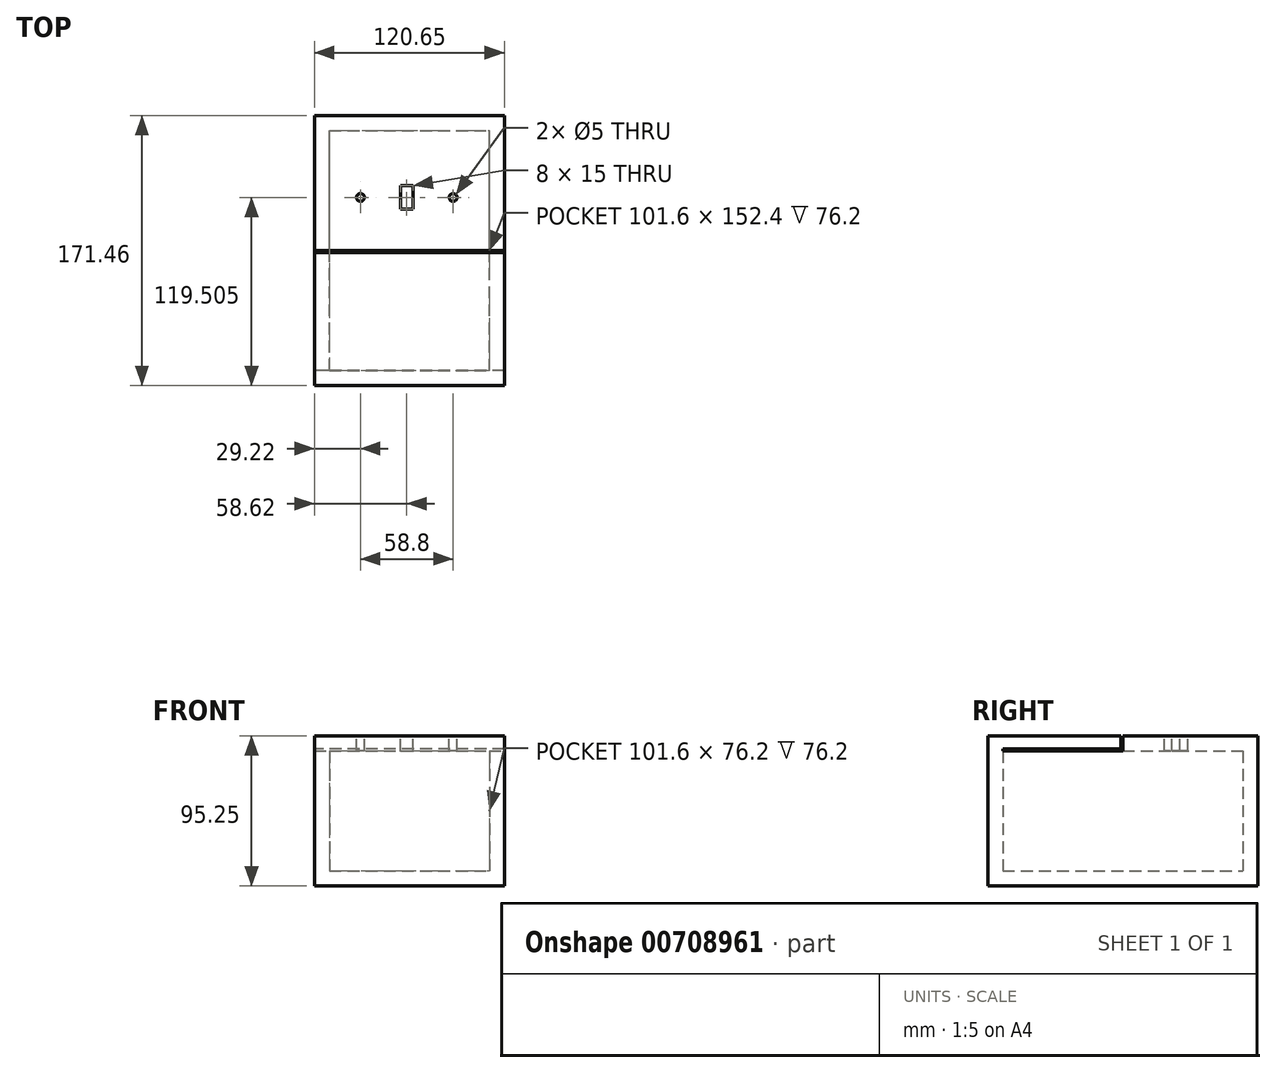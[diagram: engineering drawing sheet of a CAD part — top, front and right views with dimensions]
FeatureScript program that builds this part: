
annotation { "Feature Type Name" : "Feature", "Feature Type Description" : "" }
export const myFeature = defineFeature(function(context is Context, id is Id, definition is map)
    precondition{}
    {
        {
            var Q0;
            Q0=qCreatedBy(makeId("Front.planeOp"),FACE);
            var sketch = newSketch(context, id + "F0", { "sketchPlane" : qUnion([Q0])});
            skLineSegment(sketch, "E0.bottom", {"start": v(-49.1, 38.1) * mm, "end": v(52.5, 38.1) * mm});
            skLineSegment(sketch, "E0.top", {"start": v(-49.1, -38.1) * mm, "end": v(52.5, -38.1) * mm});
            skLineSegment(sketch, "E0.left", {"start": v(-49.1, 38.1) * mm, "end": v(-49.1, -38.1) * mm});
            skLineSegment(sketch, "E0.right", {"start": v(52.5, 38.1) * mm, "end": v(52.5, -38.1) * mm});
            skLineSegment(sketch, "E1.bottom", {"start": v(-58.62, 47.62) * mm, "end": v(62.03, 47.62) * mm});
            skLineSegment(sketch, "E1.top", {"start": v(-58.62, -47.63) * mm, "end": v(62.03, -47.63) * mm});
            skLineSegment(sketch, "E1.left", {"start": v(-58.62, 47.62) * mm, "end": v(-58.62, -47.63) * mm});
            skLineSegment(sketch, "E1.right", {"start": v(62.03, 47.62) * mm, "end": v(62.03, -47.63) * mm});
            skSolve(sketch);
        }
        {
            var Q0;
            Q0 = qSketchRegion(id + "F0", true);
            extrude(context, id + "F1", {"entities" : qUnion([Q0]), "depth" : 152.4 * mm, "offsetDistance" : 25.4 * mm});
        }
        {
            var Q0;
            Q0=makeQuery(id+"F1.opExtrude","SWEPT_FACE",FACE,{"disambiguationData":[OSD([sQuery(id+"F0.wireOp",EDGE,"E1.left")])]});
            var sketch = newSketch(context, id + "F2", { "sketchPlane" : qUnion([Q0])});
            skLineSegment(sketch, "E2.bottom", {"start": v(0, 47.63) * mm, "end": v(-9.53, 47.63) * mm});
            skLineSegment(sketch, "E2.top", {"start": v(0, -47.63) * mm, "end": v(-9.52, -47.63) * mm});
            skLineSegment(sketch, "E2.left", {"start": v(0, 47.63) * mm, "end": v(0, -47.63) * mm});
            skLineSegment(sketch, "E2.right", {"start": v(-9.53, 47.63) * mm, "end": v(-9.52, -47.63) * mm});
            skLineSegment(sketch, "E3.bottom", {"start": v(152.4, 47.63) * mm, "end": v(161.93, 47.63) * mm});
            skLineSegment(sketch, "E3.top", {"start": v(152.4, -47.63) * mm, "end": v(161.93, -47.63) * mm});
            skLineSegment(sketch, "E3.left", {"start": v(152.4, 47.63) * mm, "end": v(152.4, -47.63) * mm});
            skLineSegment(sketch, "E3.right", {"start": v(161.93, 47.63) * mm, "end": v(161.93, -47.63) * mm});
            skSolve(sketch);
        }
        {
            var Q0;
            Q0 = qSketchRegion(id + "F2", true);
            extrude(context, id + "F3", {"entities" : qUnion([Q0]), "operationType" : NewBodyOperationType.ADD, "oppositeDirection" : true, "depth" : 120.65 * mm, "offsetDistance" : 25.4 * mm});
        }
        {
            var Q0;
            Q0=makeQuery(id+"F3.boolean.opBoolean","MERGE",FACE,{"derivedFrom":[makeQuery(id+"F1.opExtrude","SWEPT_FACE",FACE,{"disambiguationData":[OSD([sQuery(id+"F0.wireOp",EDGE,"E1.bottom")])]}),makeQuery(id+"F3.opExtrude","SWEPT_FACE",FACE,{"disambiguationData":[OSD([sQuery(id+"F2.wireOp",EDGE,"E2.bottom")])]}),makeQuery(id+"F3.opExtrude","SWEPT_FACE",FACE,{"disambiguationData":[OSD([sQuery(id+"F2.wireOp",EDGE,"E3.bottom")])]})]});
            var sketch = newSketch(context, id + "F4", { "sketchPlane" : qUnion([Q0])});
            skLineSegment(sketch, "E4.bottom", {"start": v(-58.62, -76.2) * mm, "end": v(62.03, -76.2) * mm});
            skLineSegment(sketch, "E4.top", {"start": v(-58.62, -77.47) * mm, "end": v(62.03, -77.47) * mm});
            skLineSegment(sketch, "E4.left", {"start": v(-58.62, -76.2) * mm, "end": v(-58.62, -77.47) * mm});
            skLineSegment(sketch, "E4.right", {"start": v(62.03, -76.2) * mm, "end": v(62.03, -77.47) * mm});
            skSolve(sketch);
        }
        {
            var Q0;
            Q0 = qSketchRegion(id + "F4", true);
            extrude(context, id + "F5", {"entities" : qUnion([Q0]), "operationType" : NewBodyOperationType.REMOVE, "oppositeDirection" : true, "depth" : 9.52 * mm, "offsetDistance" : 25.4 * mm});
        }
        {
            var Q0;
            {var subQ0=sQuery(id+"F2.wireOp",EDGE,"E2.right");var subQ3=sQuery(id+"F2.wireOp",EDGE,"E2.bottom");var subQ7=sQuery(id+"F2.wireOp",EDGE,"E3.bottom");Q0=makeQuery(id+"F5.boolean.opBoolean","SPLIT",FACE,{"disambiguationData":[TD([makeQuery(id+"F3.opExtrude","SWEPT_FACE",FACE,{"disambiguationData":[OSD([subQ0])]})])],"derivedFrom":makeQuery(id+"F3.boolean.opBoolean","MERGE",FACE,{"derivedFrom":[makeQuery(id+"F1.opExtrude","SWEPT_FACE",FACE,{"disambiguationData":[OSD([sQuery(id+"F0.wireOp",EDGE,"E1.bottom")])]}),makeQuery(id+"F3.opExtrude","SWEPT_FACE",FACE,{"disambiguationData":[OSD([subQ3])]}),makeQuery(id+"F3.opExtrude","SWEPT_FACE",FACE,{"disambiguationData":[OSD([subQ7])]})]})});}
            var sketch = newSketch(context, id + "F6", { "sketchPlane" : qUnion([Q0])});
            skLineSegment(sketch, "E5.bottom", {"start": v(-4, -34.92) * mm, "end": v(4, -34.92) * mm});
            skLineSegment(sketch, "E5.top", {"start": v(-4, -49.93) * mm, "end": v(4, -49.92) * mm});
            skLineSegment(sketch, "E5.left", {"start": v(-4, -34.92) * mm, "end": v(-4, -49.93) * mm});
            skLineSegment(sketch, "E5.right", {"start": v(4, -34.92) * mm, "end": v(4, -49.92) * mm});
            skCircle(sketch, "E6", {"center": v(-29.4, -42.43) * mm, "radius": 2.5 * mm});
            skCircle(sketch, "E7", {"center": v(29.4, -42.42) * mm, "radius": 2.5 * mm});
            skSolve(sketch);
        }
        {
            var Q0;
            Q0 = qSketchRegion(id + "F6", true);
            extrude(context, id + "F7", {"entities" : qUnion([Q0]), "operationType" : NewBodyOperationType.REMOVE, "oppositeDirection" : true, "depth" : 25.4 * mm, "offsetDistance" : 25.4 * mm});
        }
        {
            var Q0;
            Q0=makeQuery(id+"F3.boolean.opBoolean","MERGE",FACE,{"derivedFrom":[makeQuery(id+"F1.opExtrude","SWEPT_FACE",FACE,{"disambiguationData":[OSD([sQuery(id+"F0.wireOp",EDGE,"E1.left")])]}),makeQuery(id+"F3.opExtrude","CAP_FACE",FACE,{"disambiguationData":[OSD([sQuery(id+"F2.wireOp",EDGE,"E2.bottom"),sQuery(id+"F2.wireOp",EDGE,"E2.top"),sQuery(id+"F2.wireOp",EDGE,"E2.left"),sQuery(id+"F2.wireOp",EDGE,"E2.right")])],"isStart":true}),makeQuery(id+"F3.opExtrude","CAP_FACE",FACE,{"disambiguationData":[OSD([sQuery(id+"F2.wireOp",EDGE,"E3.bottom"),sQuery(id+"F2.wireOp",EDGE,"E3.top"),sQuery(id+"F2.wireOp",EDGE,"E3.left"),sQuery(id+"F2.wireOp",EDGE,"E3.right")])],"isStart":true})]});
            var sketch = newSketch(context, id + "F8", { "sketchPlane" : qUnion([Q0])});
            skPoint(sketch, "E8.oppositeSnap0", {"position": v(67.95, 39.37) * mm});
            skLineSegment(sketch, "E8.bottom", {"start": v(77.47, 38.1) * mm, "end": v(152.4, 38.1) * mm});
            skLineSegment(sketch, "E8.top", {"start": v(77.47, 39.37) * mm, "end": v(152.4, 39.37) * mm});
            skLineSegment(sketch, "E8.left", {"start": v(77.47, 38.1) * mm, "end": v(77.47, 39.37) * mm});
            skLineSegment(sketch, "E8.right", {"start": v(152.4, 38.1) * mm, "end": v(152.4, 39.37) * mm});
            skSolve(sketch);
        }
        {
            var Q0;
            Q0 = qSketchRegion(id + "F8", true);
            extrude(context, id + "F9", {"entities" : qUnion([Q0]), "operationType" : NewBodyOperationType.REMOVE, "oppositeDirection" : true, "depth" : 179.07 * mm, "offsetDistance" : 25.4 * mm});
        }
    });
